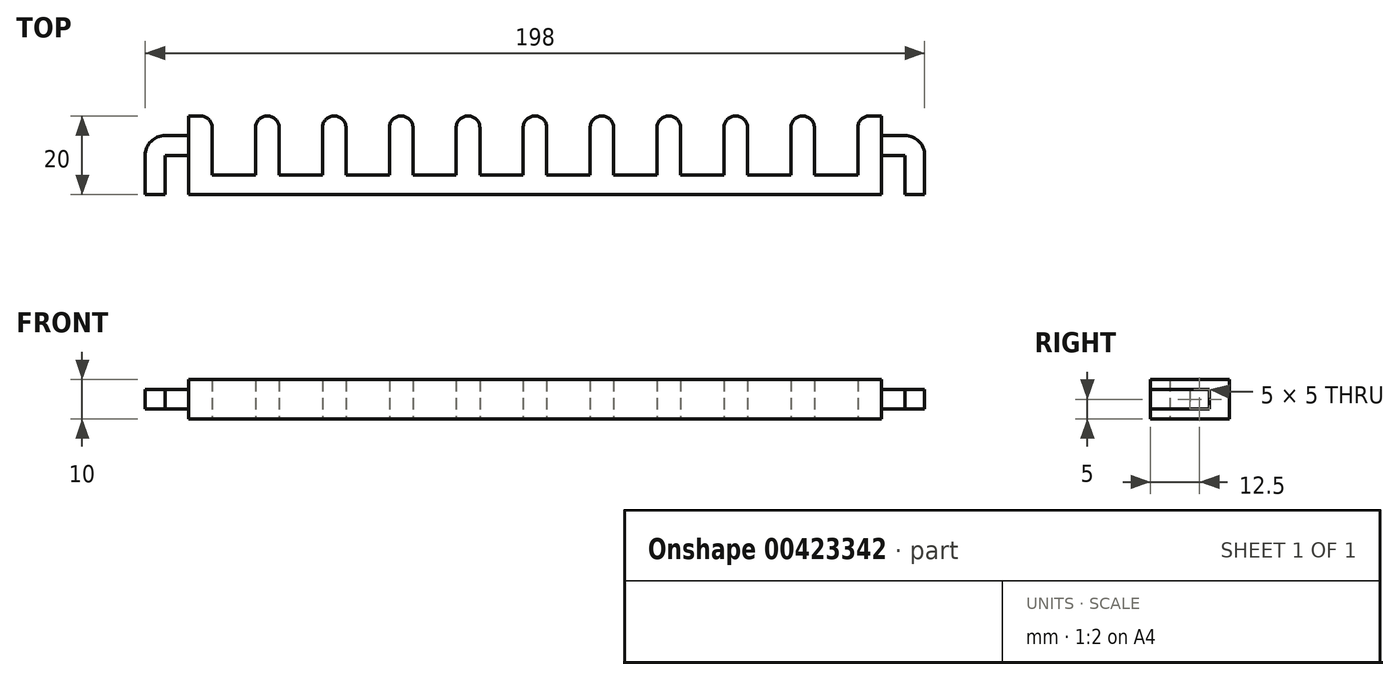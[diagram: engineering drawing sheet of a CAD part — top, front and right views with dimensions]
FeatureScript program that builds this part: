
annotation { "Feature Type Name" : "Feature", "Feature Type Description" : "" }
export const myFeature = defineFeature(function(context is Context, id is Id, definition is map)
    precondition{}
    {
        {
            var Q0;
            Q0=qCreatedBy(makeId("Top.planeOp"),FACE);
            var sketch = newSketch(context, id + "F0", { "sketchPlane" : qUnion([Q0])});
            skLineSegment(sketch, "E0.bottom", {"start": v(83, 15) * mm, "end": v(-93, 15) * mm});
            skLineSegment(sketch, "E0.top", {"start": v(83, -5) * mm, "end": v(-93, -5) * mm});
            skLineSegment(sketch, "E0.left", {"start": v(83, 15) * mm, "end": v(83, -5) * mm});
            skLineSegment(sketch, "E0.right", {"start": v(-93, 15) * mm, "end": v(-93, -5) * mm});
            skPoint(sketch, "E0.middle", {"position": v(-5, 5) * mm});
            skLineSegment(sketch, "E1.bottom", {"start": v(-87, 15) * mm, "end": v(-76, 15) * mm});
            skLineSegment(sketch, "E1.top", {"start": v(-87, 0) * mm, "end": v(-76, 0) * mm});
            skLineSegment(sketch, "E1.left", {"start": v(-87, 15) * mm, "end": v(-87, 0) * mm});
            skLineSegment(sketch, "E1.right", {"start": v(-76, 15) * mm, "end": v(-76, 0) * mm});
            skLineSegment(sketch, "E2.1.0.0", {"start": v(-59, 15) * mm, "end": v(-59, 0) * mm});
            skLineSegment(sketch, "E2.1.0.1", {"start": v(-70, 0) * mm, "end": v(-59, 0) * mm});
            skLineSegment(sketch, "E2.1.0.2", {"start": v(-70, 15) * mm, "end": v(-70, 0) * mm});
            skLineSegment(sketch, "E2.1.0.3", {"start": v(-70, 15) * mm, "end": v(-59, 15) * mm});
            skLineSegment(sketch, "E2.2.0.0", {"start": v(-42, 15) * mm, "end": v(-42, 0) * mm});
            skLineSegment(sketch, "E2.2.0.1", {"start": v(-53, 0) * mm, "end": v(-42, 0) * mm});
            skLineSegment(sketch, "E2.2.0.2", {"start": v(-53, 15) * mm, "end": v(-53, 0) * mm});
            skLineSegment(sketch, "E2.2.0.3", {"start": v(-53, 15) * mm, "end": v(-42, 15) * mm});
            skLineSegment(sketch, "E2.3.0.0", {"start": v(-25, 15) * mm, "end": v(-25, 0) * mm});
            skLineSegment(sketch, "E2.3.0.1", {"start": v(-36, 0) * mm, "end": v(-25, 0) * mm});
            skLineSegment(sketch, "E2.3.0.2", {"start": v(-36, 15) * mm, "end": v(-36, 0) * mm});
            skLineSegment(sketch, "E2.3.0.3", {"start": v(-36, 15) * mm, "end": v(-25, 15) * mm});
            skLineSegment(sketch, "E2.4.0.0", {"start": v(-8, 15) * mm, "end": v(-8, 0) * mm});
            skLineSegment(sketch, "E2.4.0.1", {"start": v(-19, 0) * mm, "end": v(-8, 0) * mm});
            skLineSegment(sketch, "E2.4.0.2", {"start": v(-19, 15) * mm, "end": v(-19, 0) * mm});
            skLineSegment(sketch, "E2.4.0.3", {"start": v(-19, 15) * mm, "end": v(-8, 15) * mm});
            skLineSegment(sketch, "E2.5.0.0", {"start": v(9, 15) * mm, "end": v(9, 0) * mm});
            skLineSegment(sketch, "E2.5.0.1", {"start": v(-2, 0) * mm, "end": v(9, 0) * mm});
            skLineSegment(sketch, "E2.5.0.2", {"start": v(-2, 15) * mm, "end": v(-2, 0) * mm});
            skLineSegment(sketch, "E2.5.0.3", {"start": v(-2, 15) * mm, "end": v(9, 15) * mm});
            skLineSegment(sketch, "E2.6.0.0", {"start": v(26, 15) * mm, "end": v(26, 0) * mm});
            skLineSegment(sketch, "E2.6.0.1", {"start": v(15, 0) * mm, "end": v(26, 0) * mm});
            skLineSegment(sketch, "E2.6.0.2", {"start": v(15, 15) * mm, "end": v(15, 0) * mm});
            skLineSegment(sketch, "E2.6.0.3", {"start": v(15, 15) * mm, "end": v(26, 15) * mm});
            skLineSegment(sketch, "E2.7.0.0", {"start": v(43, 15) * mm, "end": v(43, 0) * mm});
            skLineSegment(sketch, "E2.7.0.1", {"start": v(32, 0) * mm, "end": v(43, 0) * mm});
            skLineSegment(sketch, "E2.7.0.2", {"start": v(32, 15) * mm, "end": v(32, 0) * mm});
            skLineSegment(sketch, "E2.7.0.3", {"start": v(32, 15) * mm, "end": v(43, 15) * mm});
            skLineSegment(sketch, "E2.8.0.0", {"start": v(60, 15) * mm, "end": v(60, 0) * mm});
            skLineSegment(sketch, "E2.8.0.1", {"start": v(49, 0) * mm, "end": v(60, 0) * mm});
            skLineSegment(sketch, "E2.8.0.2", {"start": v(49, 15) * mm, "end": v(49, 0) * mm});
            skLineSegment(sketch, "E2.8.0.3", {"start": v(49, 15) * mm, "end": v(60, 15) * mm});
            skLineSegment(sketch, "E2.9.0.0", {"start": v(77, 15) * mm, "end": v(77, 0) * mm});
            skLineSegment(sketch, "E2.9.0.1", {"start": v(66, 0) * mm, "end": v(77, 0) * mm});
            skLineSegment(sketch, "E2.9.0.2", {"start": v(66, 15) * mm, "end": v(66, 0) * mm});
            skLineSegment(sketch, "E2.9.0.3", {"start": v(66, 15) * mm, "end": v(77, 15) * mm});
            skLineSegment(sketch, "E2.direction1", {"start": v(-76, 0) * mm, "end": v(-59, 0) * mm, "construction": true});
            skSolve(sketch);
        }
        {
            var Q0;
            Q0=makeQuery(id+"F0.imprint","IMPRINT",FACE,{"disambiguationData":[TD([[makeQuery(id+"F0.imprint","IMPRINT",EDGE,{"derivedFrom":sQuery(id+"F0.wireOp",EDGE,"E0.top")}),-1.0]])]});
            extrude(context, id + "F1", {"entities" : qUnion([Q0]), "depth" : 10 * mm});
        }
        {
            var Q0;
            Q0=makeQuery(id+"F1.opExtrude","SWEPT_FACE",FACE,{"disambiguationData":[OSD([sQuery(id+"F0.wireOp",EDGE,"E0.right")])]});
            var sketch = newSketch(context, id + "F2", { "sketchPlane" : qUnion([Q0])});
            skLineSegment(sketch, "E3.bottom", {"start": v(-10, 7.5) * mm, "end": v(-5, 7.5) * mm});
            skLineSegment(sketch, "E3.top", {"start": v(-10, 2.5) * mm, "end": v(-5, 2.5) * mm});
            skLineSegment(sketch, "E3.left", {"start": v(-10, 7.5) * mm, "end": v(-10, 2.5) * mm});
            skLineSegment(sketch, "E3.right", {"start": v(-5, 7.5) * mm, "end": v(-5, 2.5) * mm});
            skSolve(sketch);
        }
        {
            var Q0;
            Q0=makeQuery(id+"F2.imprint","IMPRINT",FACE,{"disambiguationData":[TD([[makeQuery(id+"F2.imprint","IMPRINT",EDGE,{"derivedFrom":sQuery(id+"F2.wireOp",EDGE,"E3.bottom")}),-1.0]])]});
            extrude(context, id + "F3", {"entities" : qUnion([Q0]), "operationType" : NewBodyOperationType.ADD, "depth" : 11 * mm});
        }
        {
            var Q0;
            Q0=makeQuery(id+"F3.opExtrude","SWEPT_FACE",FACE,{"disambiguationData":[OSD([sQuery(id+"F2.wireOp",EDGE,"E3.right")])]});
            var sketch = newSketch(context, id + "F4", { "sketchPlane" : qUnion([Q0])});
            skLineSegment(sketch, "E4.bottom", {"start": v(-104, 7.5) * mm, "end": v(-99, 7.5) * mm});
            skLineSegment(sketch, "E4.top", {"start": v(-104, 2.5) * mm, "end": v(-99, 2.5) * mm});
            skLineSegment(sketch, "E4.left", {"start": v(-104, 7.5) * mm, "end": v(-104, 2.5) * mm});
            skLineSegment(sketch, "E4.right", {"start": v(-99, 7.5) * mm, "end": v(-99, 2.5) * mm});
            skSolve(sketch);
        }
        {
            var Q0;
            Q0 = qSketchRegion(id + "F4", true);
            extrude(context, id + "F5", {"entities" : qUnion([Q0]), "operationType" : NewBodyOperationType.ADD, "depth" : 10 * mm});
        }
        {
            var Q0;
            Q0=makeQuery(id+"F1.opExtrude","SWEPT_EDGE",EDGE,{"disambiguationData":[OSD([sQuery(id+"F0.wireOp",EDGE,"E0.bottom"),sQuery(id+"F0.wireOp",EDGE,"E1.bottom"),sQuery(id+"F0.wireOp",EDGE,"E1.left")])]});
            var Q1;
            Q1=makeQuery(id+"F1.opExtrude","SWEPT_EDGE",EDGE,{"disambiguationData":[OSD([sQuery(id+"F0.wireOp",EDGE,"E0.bottom"),sQuery(id+"F0.wireOp",EDGE,"E1.bottom"),sQuery(id+"F0.wireOp",EDGE,"E1.right")])]});
            var Q2;
            Q2=makeQuery(id+"F1.opExtrude","SWEPT_EDGE",EDGE,{"disambiguationData":[OSD([sQuery(id+"F0.wireOp",EDGE,"E0.bottom"),sQuery(id+"F0.wireOp",EDGE,"E2.1.0.2"),sQuery(id+"F0.wireOp",EDGE,"E2.1.0.3")])]});
            var Q3;
            Q3=makeQuery(id+"F1.opExtrude","SWEPT_EDGE",EDGE,{"disambiguationData":[OSD([sQuery(id+"F0.wireOp",EDGE,"E0.bottom"),sQuery(id+"F0.wireOp",EDGE,"E2.1.0.0"),sQuery(id+"F0.wireOp",EDGE,"E2.1.0.3")])]});
            var Q4;
            Q4=makeQuery(id+"F1.opExtrude","SWEPT_EDGE",EDGE,{"disambiguationData":[OSD([sQuery(id+"F0.wireOp",EDGE,"E0.bottom"),sQuery(id+"F0.wireOp",EDGE,"E2.2.0.2"),sQuery(id+"F0.wireOp",EDGE,"E2.2.0.3")])]});
            var Q5;
            Q5=makeQuery(id+"F1.opExtrude","SWEPT_EDGE",EDGE,{"disambiguationData":[OSD([sQuery(id+"F0.wireOp",EDGE,"E0.bottom"),sQuery(id+"F0.wireOp",EDGE,"E2.2.0.0"),sQuery(id+"F0.wireOp",EDGE,"E2.2.0.3")])]});
            var Q6;
            Q6=makeQuery(id+"F1.opExtrude","SWEPT_EDGE",EDGE,{"disambiguationData":[OSD([sQuery(id+"F0.wireOp",EDGE,"E0.bottom"),sQuery(id+"F0.wireOp",EDGE,"E2.3.0.2"),sQuery(id+"F0.wireOp",EDGE,"E2.3.0.3")])]});
            var Q7;
            Q7=makeQuery(id+"F1.opExtrude","SWEPT_EDGE",EDGE,{"disambiguationData":[OSD([sQuery(id+"F0.wireOp",EDGE,"E0.bottom"),sQuery(id+"F0.wireOp",EDGE,"E2.3.0.0"),sQuery(id+"F0.wireOp",EDGE,"E2.3.0.3")])]});
            var Q8;
            Q8=makeQuery(id+"F1.opExtrude","SWEPT_EDGE",EDGE,{"disambiguationData":[OSD([sQuery(id+"F0.wireOp",EDGE,"E0.bottom"),sQuery(id+"F0.wireOp",EDGE,"E2.4.0.2"),sQuery(id+"F0.wireOp",EDGE,"E2.4.0.3")])]});
            var Q9;
            Q9=makeQuery(id+"F1.opExtrude","SWEPT_EDGE",EDGE,{"disambiguationData":[OSD([sQuery(id+"F0.wireOp",EDGE,"E0.bottom"),sQuery(id+"F0.wireOp",EDGE,"E2.4.0.0"),sQuery(id+"F0.wireOp",EDGE,"E2.4.0.3")])]});
            var Q10;
            Q10=makeQuery(id+"F1.opExtrude","SWEPT_EDGE",EDGE,{"disambiguationData":[OSD([sQuery(id+"F0.wireOp",EDGE,"E0.bottom"),sQuery(id+"F0.wireOp",EDGE,"E2.5.0.2"),sQuery(id+"F0.wireOp",EDGE,"E2.5.0.3")])]});
            var Q11;
            Q11=makeQuery(id+"F1.opExtrude","SWEPT_EDGE",EDGE,{"disambiguationData":[OSD([sQuery(id+"F0.wireOp",EDGE,"E0.bottom"),sQuery(id+"F0.wireOp",EDGE,"E2.5.0.0"),sQuery(id+"F0.wireOp",EDGE,"E2.5.0.3")])]});
            var Q12;
            Q12=makeQuery(id+"F1.opExtrude","SWEPT_EDGE",EDGE,{"disambiguationData":[OSD([sQuery(id+"F0.wireOp",EDGE,"E0.bottom"),sQuery(id+"F0.wireOp",EDGE,"E2.6.0.2"),sQuery(id+"F0.wireOp",EDGE,"E2.6.0.3")])]});
            var Q13;
            Q13=makeQuery(id+"F1.opExtrude","SWEPT_EDGE",EDGE,{"disambiguationData":[OSD([sQuery(id+"F0.wireOp",EDGE,"E0.bottom"),sQuery(id+"F0.wireOp",EDGE,"E2.6.0.0"),sQuery(id+"F0.wireOp",EDGE,"E2.6.0.3")])]});
            var Q14;
            Q14=makeQuery(id+"F1.opExtrude","SWEPT_EDGE",EDGE,{"disambiguationData":[OSD([sQuery(id+"F0.wireOp",EDGE,"E0.bottom"),sQuery(id+"F0.wireOp",EDGE,"E2.7.0.2"),sQuery(id+"F0.wireOp",EDGE,"E2.7.0.3")])]});
            var Q15;
            Q15=makeQuery(id+"F1.opExtrude","SWEPT_EDGE",EDGE,{"disambiguationData":[OSD([sQuery(id+"F0.wireOp",EDGE,"E0.bottom"),sQuery(id+"F0.wireOp",EDGE,"E2.7.0.0"),sQuery(id+"F0.wireOp",EDGE,"E2.7.0.3")])]});
            var Q16;
            Q16=makeQuery(id+"F1.opExtrude","SWEPT_EDGE",EDGE,{"disambiguationData":[OSD([sQuery(id+"F0.wireOp",EDGE,"E0.bottom"),sQuery(id+"F0.wireOp",EDGE,"E2.8.0.2"),sQuery(id+"F0.wireOp",EDGE,"E2.8.0.3")])]});
            var Q17;
            Q17=makeQuery(id+"F1.opExtrude","SWEPT_EDGE",EDGE,{"disambiguationData":[OSD([sQuery(id+"F0.wireOp",EDGE,"E0.bottom"),sQuery(id+"F0.wireOp",EDGE,"E2.8.0.0"),sQuery(id+"F0.wireOp",EDGE,"E2.8.0.3")])]});
            var Q18;
            Q18=makeQuery(id+"F1.opExtrude","SWEPT_EDGE",EDGE,{"disambiguationData":[OSD([sQuery(id+"F0.wireOp",EDGE,"E0.bottom"),sQuery(id+"F0.wireOp",EDGE,"E2.9.0.2"),sQuery(id+"F0.wireOp",EDGE,"E2.9.0.3")])]});
            var Q19;
            Q19=makeQuery(id+"F1.opExtrude","SWEPT_EDGE",EDGE,{"disambiguationData":[OSD([sQuery(id+"F0.wireOp",EDGE,"E0.bottom"),sQuery(id+"F0.wireOp",EDGE,"E2.9.0.0"),sQuery(id+"F0.wireOp",EDGE,"E2.9.0.3")])]});
            fillet(context, id + "F6", {"entities" : qUnion([Q0, Q1, Q2, Q3, Q4, Q5, Q6, Q7, Q8, Q9, Q10, Q11, Q12, Q13, Q14, Q15, Q16, Q17, Q18, Q19]), "radius" : 3 * mm, "tangentPropagation" : true, "allowEdgeOverflow" : false});
        }
        {
            var Q0;
            Q0=makeQuery(id+"F3.opExtrude","CAP_EDGE",EDGE,{"disambiguationData":[OSD([sQuery(id+"F2.wireOp",EDGE,"E3.left")])],"isStart":false});
            fillet(context, id + "F7", {"entities" : qUnion([Q0]), "radius" : 5 * mm, "tangentPropagation" : true, "allowEdgeOverflow" : false});
        }
        {
            var Q0;
            Q0=makeQuery(id+"F1.opExtrude","SWEPT_FACE",FACE,{"disambiguationData":[OSD([sQuery(id+"F0.wireOp",EDGE,"E0.left")])]});
            var sketch = newSketch(context, id + "F8", { "sketchPlane" : qUnion([Q0])});
            skLineSegment(sketch, "E5.bottom", {"start": v(5, 7.5) * mm, "end": v(10, 7.5) * mm});
            skLineSegment(sketch, "E5.top", {"start": v(5, 2.5) * mm, "end": v(10, 2.5) * mm});
            skLineSegment(sketch, "E5.left", {"start": v(5, 7.5) * mm, "end": v(5, 2.5) * mm});
            skLineSegment(sketch, "E5.right", {"start": v(10, 7.5) * mm, "end": v(10, 2.5) * mm});
            skSolve(sketch);
        }
        {
            var Q0;
            Q0=makeQuery(id+"F8.imprint","IMPRINT",FACE,{"disambiguationData":[TD([[makeQuery(id+"F8.imprint","IMPRINT",EDGE,{"derivedFrom":sQuery(id+"F8.wireOp",EDGE,"E5.bottom")}),-1.0]])]});
            extrude(context, id + "F9", {"entities" : qUnion([Q0]), "operationType" : NewBodyOperationType.ADD, "depth" : 11 * mm});
        }
        {
            var Q0;
            Q0=makeQuery(id+"F9.opExtrude","SWEPT_FACE",FACE,{"disambiguationData":[OSD([sQuery(id+"F8.wireOp",EDGE,"E5.left")])]});
            var sketch = newSketch(context, id + "F10", { "sketchPlane" : qUnion([Q0])});
            skLineSegment(sketch, "E6.bottom", {"start": v(94, 7.5) * mm, "end": v(89, 7.5) * mm});
            skLineSegment(sketch, "E6.top", {"start": v(94, 2.5) * mm, "end": v(89, 2.5) * mm});
            skLineSegment(sketch, "E6.left", {"start": v(94, 7.5) * mm, "end": v(94, 2.5) * mm});
            skLineSegment(sketch, "E6.right", {"start": v(89, 7.5) * mm, "end": v(89, 2.5) * mm});
            skSolve(sketch);
        }
        {
            var Q0;
            Q0=makeQuery(id+"F10.imprint","IMPRINT",FACE,{"disambiguationData":[TD([[makeQuery(id+"F10.imprint","IMPRINT",EDGE,{"derivedFrom":sQuery(id+"F10.wireOp",EDGE,"E6.bottom")}),1.0]])]});
            extrude(context, id + "F11", {"entities" : qUnion([Q0]), "operationType" : NewBodyOperationType.ADD, "depth" : 10 * mm});
        }
        {
            var Q0;
            Q0=makeQuery(id+"F9.opExtrude","CAP_EDGE",EDGE,{"disambiguationData":[OSD([sQuery(id+"F8.wireOp",EDGE,"E5.right")])],"isStart":false});
            fillet(context, id + "F12", {"entities" : qUnion([Q0]), "radius" : 5 * mm, "tangentPropagation" : true, "allowEdgeOverflow" : false});
        }
    });
